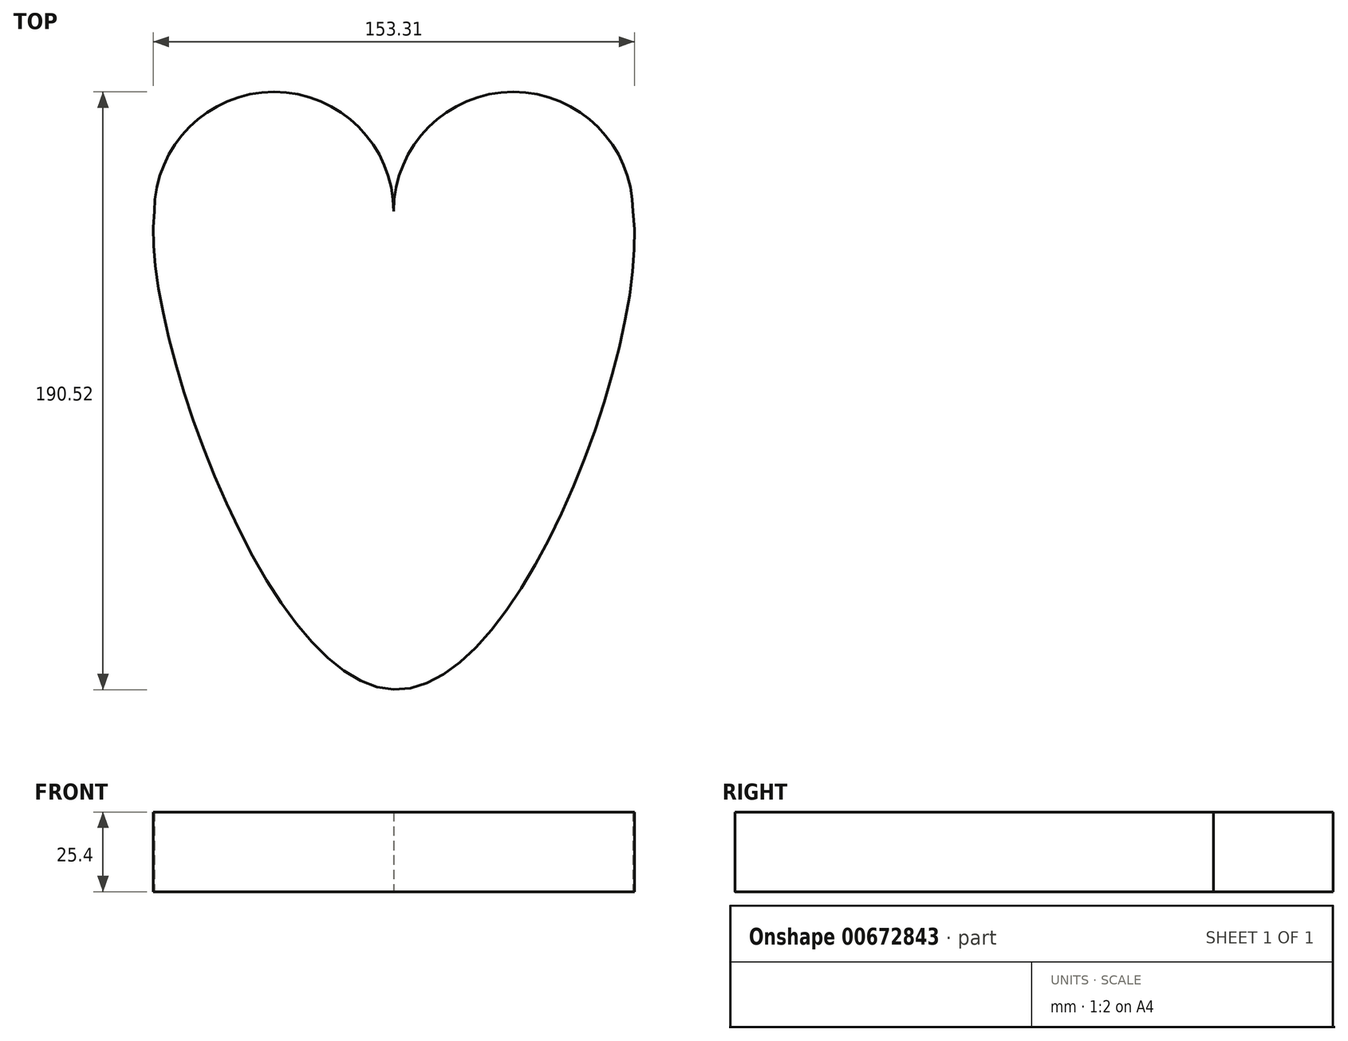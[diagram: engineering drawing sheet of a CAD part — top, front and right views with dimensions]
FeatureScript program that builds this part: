
annotation { "Feature Type Name" : "Feature", "Feature Type Description" : "" }
export const myFeature = defineFeature(function(context is Context, id is Id, definition is map)
    precondition{}
    {
        {
            var Q0;
            Q0=qCreatedBy(makeId("Top.planeOp"),FACE);
            var sketch = newSketch(context, id + "F0", { "sketchPlane" : qUnion([Q0])});
            skLineSegment(sketch, "E0", {"start": v(-74.5, 10.7) * mm, "end": v(77.9, 10.7) * mm});
            skPoint(sketch, "E1", {"position": v(1.7, 10.7) * mm});
            skPoint(sketch, "E2", {"position": v(-36.4, 10.7) * mm});
            skPoint(sketch, "E3", {"position": v(39.8, 10.7) * mm});
            skArc(sketch, "E4", {"start": v(1.7, 10.7) * mm, "mid": v(-36.4, 48.8) * mm, "end": v(-74.5, 10.7) * mm});
            skArc(sketch, "E5", {"start": v(77.9, 10.7) * mm, "mid": v(39.8, 48.8) * mm, "end": v(1.7, 10.7) * mm});
            skLineSegment(sketch, "E6", {"start": v(1.7, 10.7) * mm, "end": v(1.7, -141.7) * mm});
            skFitSpline(sketch, "E7", {"points": [v(-74.5, 10.7) * mm, v(1.7, -141.7) * mm, v(77.9, 10.7) * mm], "startDerivative": vector(-29.1, -209.12) * mm, "endDerivative": vector(-33.51, 242.87) * mm});
            skSolve(sketch);
        }
        {
            var Q0;
            Q0 = qSketchRegion(id + "F0", true);
            extrude(context, id + "F1", {"entities" : qUnion([Q0]), "depth" : 25.4 * mm, "offsetDistance" : 25.4 * mm});
        }
    });
